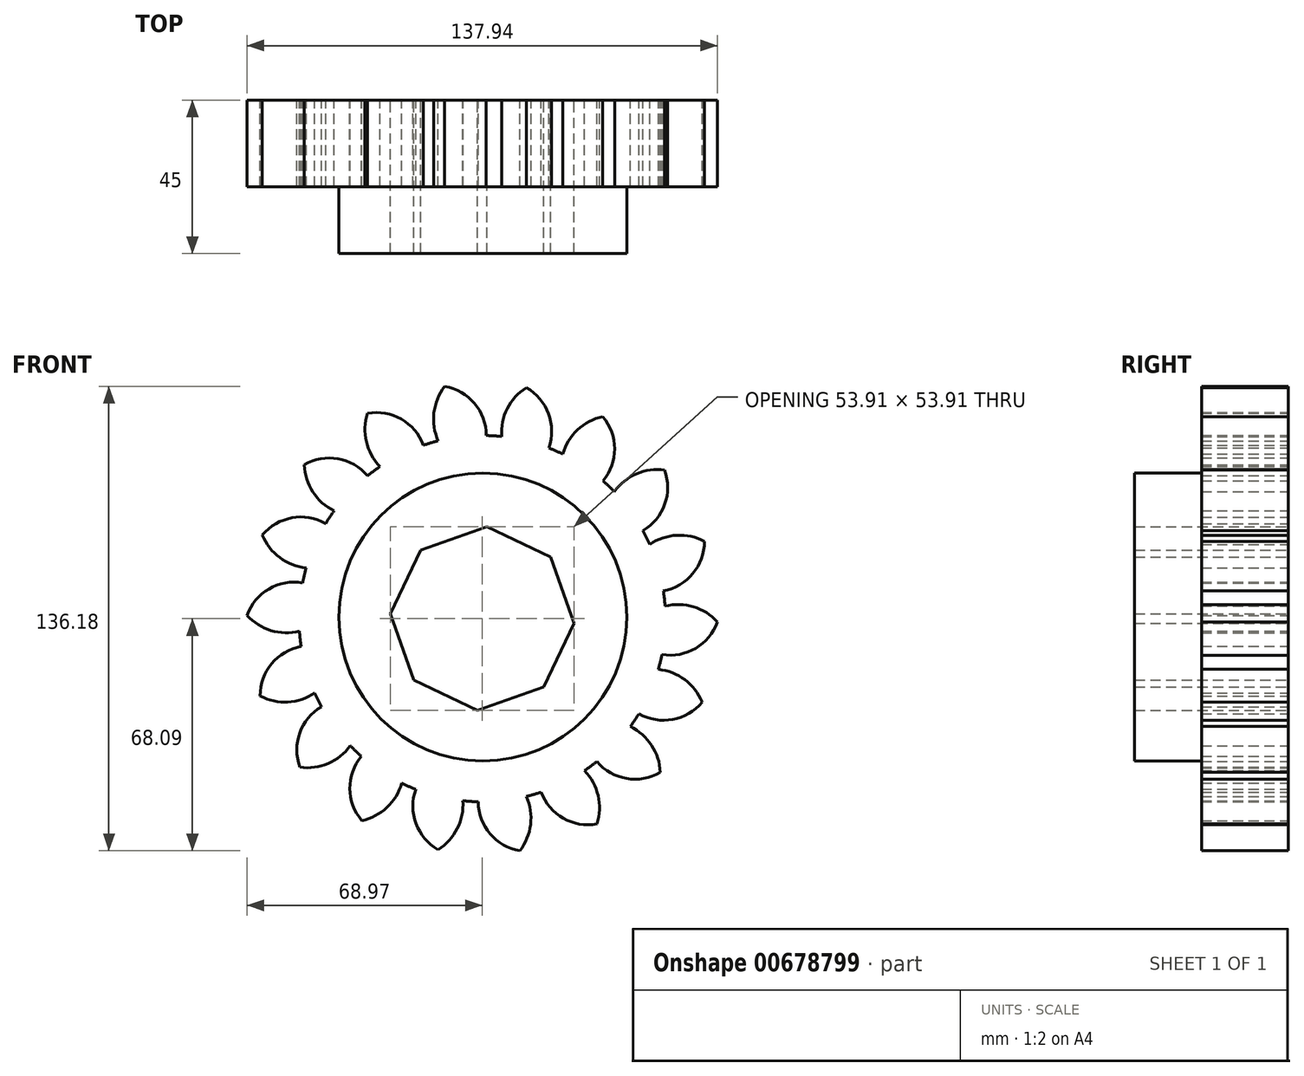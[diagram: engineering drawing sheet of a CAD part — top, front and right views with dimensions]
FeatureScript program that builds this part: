
annotation { "Feature Type Name" : "Feature", "Feature Type Description" : "" }
export const myFeature = defineFeature(function(context is Context, id is Id, definition is map)
    precondition{}
    {
        {
            var Q0;
            Q0=qCreatedBy(makeId("Front.planeOp"),FACE);
            var sketch = newSketch(context, id + "F0", { "sketchPlane" : qUnion([Q0])});
            skCircle(sketch, "E0", {"center": v(0, 0) * mm, "radius": 53.72 * mm});
            skCircle(sketch, "E1", {"center": v(0, 0) * mm, "radius": 58.67 * mm, "construction": true});
            skCircle(sketch, "E2", {"center": v(0.15, 0.46) * mm, "radius": 63.5 * mm, "construction": true});
            skLineSegment(sketch, "E3", {"start": v(0.15, 0.46) * mm, "end": v(0.15, 76.25) * mm, "construction": true});
            skLineSegment(sketch, "E4", {"start": v(0.15, 0.46) * mm, "end": v(-4.75, 75.32) * mm, "construction": true});
            skLineSegment(sketch, "E5", {"start": v(0.15, 58.67) * mm, "end": v(-64.36, 58.84) * mm, "construction": true});
            skLineSegment(sketch, "E6", {"start": v(0.15, 58.67) * mm, "end": v(-63.63, 35.65) * mm, "construction": true});
            skCircle(sketch, "E7", {"center": v(0.15, 58.67) * mm, "radius": 14.6 * mm, "construction": true});
            skCircle(sketch, "E8", {"center": v(-13.58, 53.71) * mm, "radius": 14.6 * mm, "construction": true});
            skArc(sketch, "E9", {"start": v(0.15, 58.67) * mm, "mid": v(-13.3, 74.45) * mm, "end": v(-13.58, 53.71) * mm});
            skArc(sketch, "E10", {"start": v(-11, 68.1) * mm, "mid": v(-14.18, 60.38) * mm, "end": v(-12.92, 52.14) * mm});
            skArc(sketch, "E11", {"start": v(1.2, 53.7) * mm, "mid": v(-2.3, 63.12) * mm, "end": v(-11, 68.1) * mm});
            skCircle(sketch, "E12", {"center": v(0.15, 0.46) * mm, "radius": 42.22 * mm});
            skCircle(sketch, "E13.cCircle", {"center": v(0, 0) * mm, "radius": 24.94 * mm, "construction": true});
            skLineSegment(sketch, "E13.0", {"start": v(-18.06, 20.06) * mm, "end": v(1.41, 26.95) * mm});
            skLineSegment(sketch, "E13.1", {"start": v(1.41, 26.95) * mm, "end": v(20.06, 18.06) * mm});
            skLineSegment(sketch, "E13.2", {"start": v(20.06, 18.06) * mm, "end": v(26.95, -1.41) * mm});
            skLineSegment(sketch, "E13.3", {"start": v(26.95, -1.41) * mm, "end": v(18.06, -20.06) * mm});
            skLineSegment(sketch, "E13.4", {"start": v(18.06, -20.06) * mm, "end": v(-1.41, -26.95) * mm});
            skLineSegment(sketch, "E13.5", {"start": v(-1.41, -26.95) * mm, "end": v(-20.06, -18.06) * mm});
            skLineSegment(sketch, "E13.6", {"start": v(-20.06, -18.06) * mm, "end": v(-26.95, 1.41) * mm});
            skLineSegment(sketch, "E13.7", {"start": v(-26.95, 1.41) * mm, "end": v(-18.06, 20.06) * mm});
            skPoint(sketch, "E13.0.midPoint", {"position": v(-8.32, 23.5) * mm});
            skSolve(sketch);
        }
        {
            var Q0;
            {var subQ0=sQuery(id+"F0.wireOp",EDGE,"E0");var subQ1=makeQuery(id+"F0.imprint","INTERSECT",VERTEX,{"derivedFrom":[subQ0,sQuery(id+"F0.wireOp",EDGE,"E10")]});Q0=makeQuery(id+"F0.imprint","IMPRINT",FACE,{"disambiguationData":[TD([[makeQuery(id+"F0.imprint","IMPRINT",EDGE,{"disambiguationData":[TD([[subQ1,1.0]])],"derivedFrom":subQ0}),1.0]])]});}
            var Q1;
            {var subQ0=sQuery(id+"F0.wireOp",EDGE,"E10");Q1=makeQuery(id+"F0.imprint","IMPRINT",FACE,{"disambiguationData":[TD([[makeQuery(id+"F0.imprint","IMPRINT",EDGE,{"derivedFrom":subQ0}),1.0]])]});}
            extrude(context, id + "F1", {"entities" : qUnion([Q0, Q1]), "depth" : 25.4 * mm, "offsetDistance" : 25.4 * mm});
        }
        {
            var Q0;
            Q0=makeQuery(id+"F1.opExtrude","SWEPT_BODY",BODY,{"disambiguationData":[OSD([sQuery(id+"F0.wireOp",EDGE,"E0"),sQuery(id+"F0.wireOp",EDGE,"E10"),sQuery(id+"F0.wireOp",EDGE,"E11")])]});
            var Q1;
            Q1=makeQuery(id+"F1.opExtrude","SWEPT_FACE",FACE,{"disambiguationData":[OSD([sQuery(id+"F0.wireOp",EDGE,"E0")])]});
            circularPattern(context, id + "F2", {"operationType" : NewBodyOperationType.ADD, "entities" : qUnion([Q0]), "axis" : qUnion([Q1]), "angle" : 360 * degree, "instanceCount" : 18, "equalSpace" : true});
        }
        {
            var Q0;
            Q0=makeQuery(id+"F0.imprint","IMPRINT",FACE,{"disambiguationData":[TD([[makeQuery(id+"F0.imprint","IMPRINT",EDGE,{"derivedFrom":sQuery(id+"F0.wireOp",EDGE,"E12")}),1.0]])]});
            extrude(context, id + "F3", {"entities" : qUnion([Q0]), "operationType" : NewBodyOperationType.ADD, "depth" : 45 * mm, "offsetDistance" : 25.4 * mm});
        }
    });
